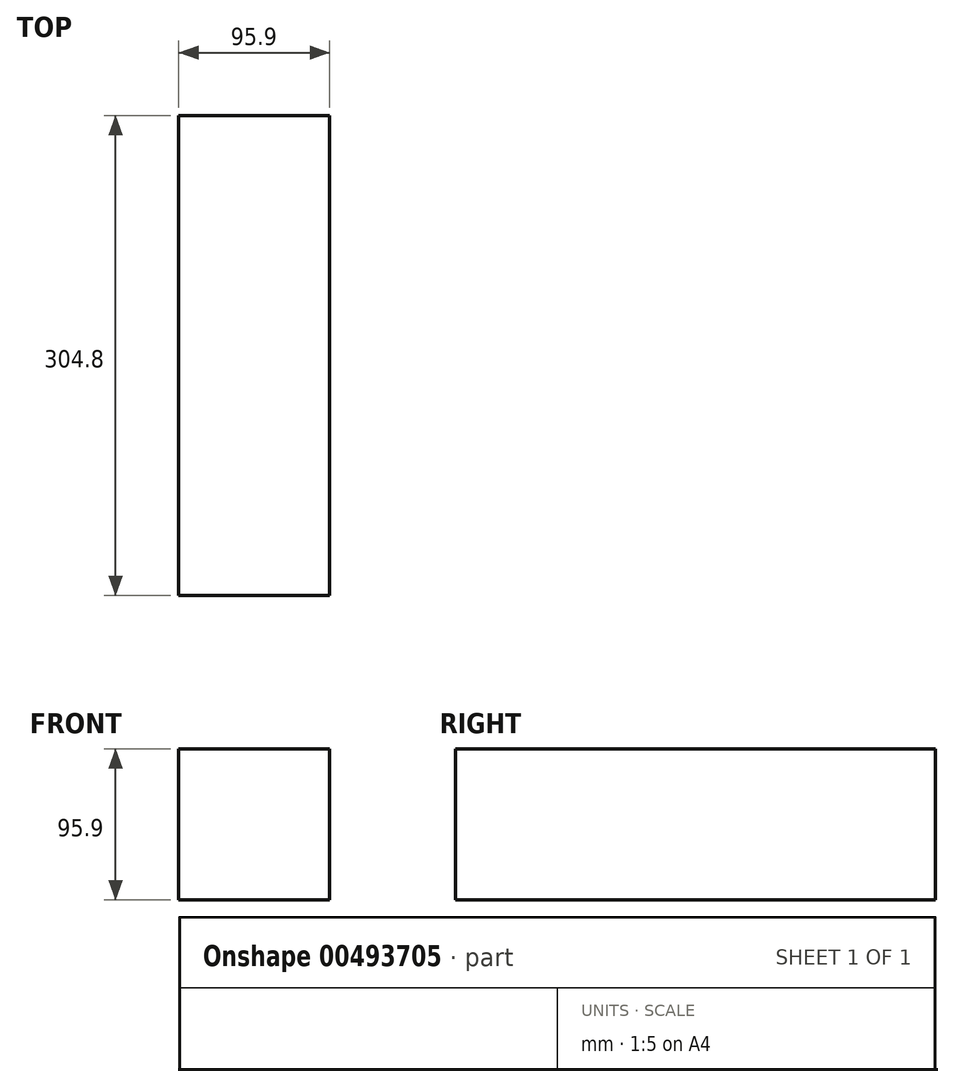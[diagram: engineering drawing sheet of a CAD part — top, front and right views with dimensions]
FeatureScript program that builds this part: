
annotation { "Feature Type Name" : "Feature", "Feature Type Description" : "" }
export const myFeature = defineFeature(function(context is Context, id is Id, definition is map)
    precondition{}
    {
        {
            var Q0;
            Q0=qCreatedBy(makeId("Front.planeOp"),FACE);
            var sketch = newSketch(context, id + "F0", { "sketchPlane" : qUnion([Q0])});
            skCircle(sketch, "E0.cCircle", {"center": v(0, 0) * mm, "radius": 47.95 * mm, "construction": true});
            skLineSegment(sketch, "E0.0", {"start": v(-47.95, 47.95) * mm, "end": v(47.95, 47.95) * mm});
            skLineSegment(sketch, "E0.1", {"start": v(47.95, 47.95) * mm, "end": v(47.95, -47.95) * mm});
            skLineSegment(sketch, "E0.2", {"start": v(47.95, -47.95) * mm, "end": v(-47.95, -47.95) * mm});
            skLineSegment(sketch, "E0.3", {"start": v(-47.95, -47.95) * mm, "end": v(-47.95, 47.95) * mm});
            skPoint(sketch, "E0.0.midPoint", {"position": v(0, 47.95) * mm});
            skSolve(sketch);
        }
        {
            var Q0;
            Q0=makeQuery(id+"F0.imprint","IMPRINT",FACE,{"disambiguationData":[TD([[makeQuery(id+"F0.imprint","IMPRINT",EDGE,{"derivedFrom":sQuery(id+"F0.wireOp",EDGE,"E0.0")}),-1.0]])]});
            extrude(context, id + "F1", {"entities" : qUnion([Q0]), "depth" : 304.8 * mm});
        }
    });
